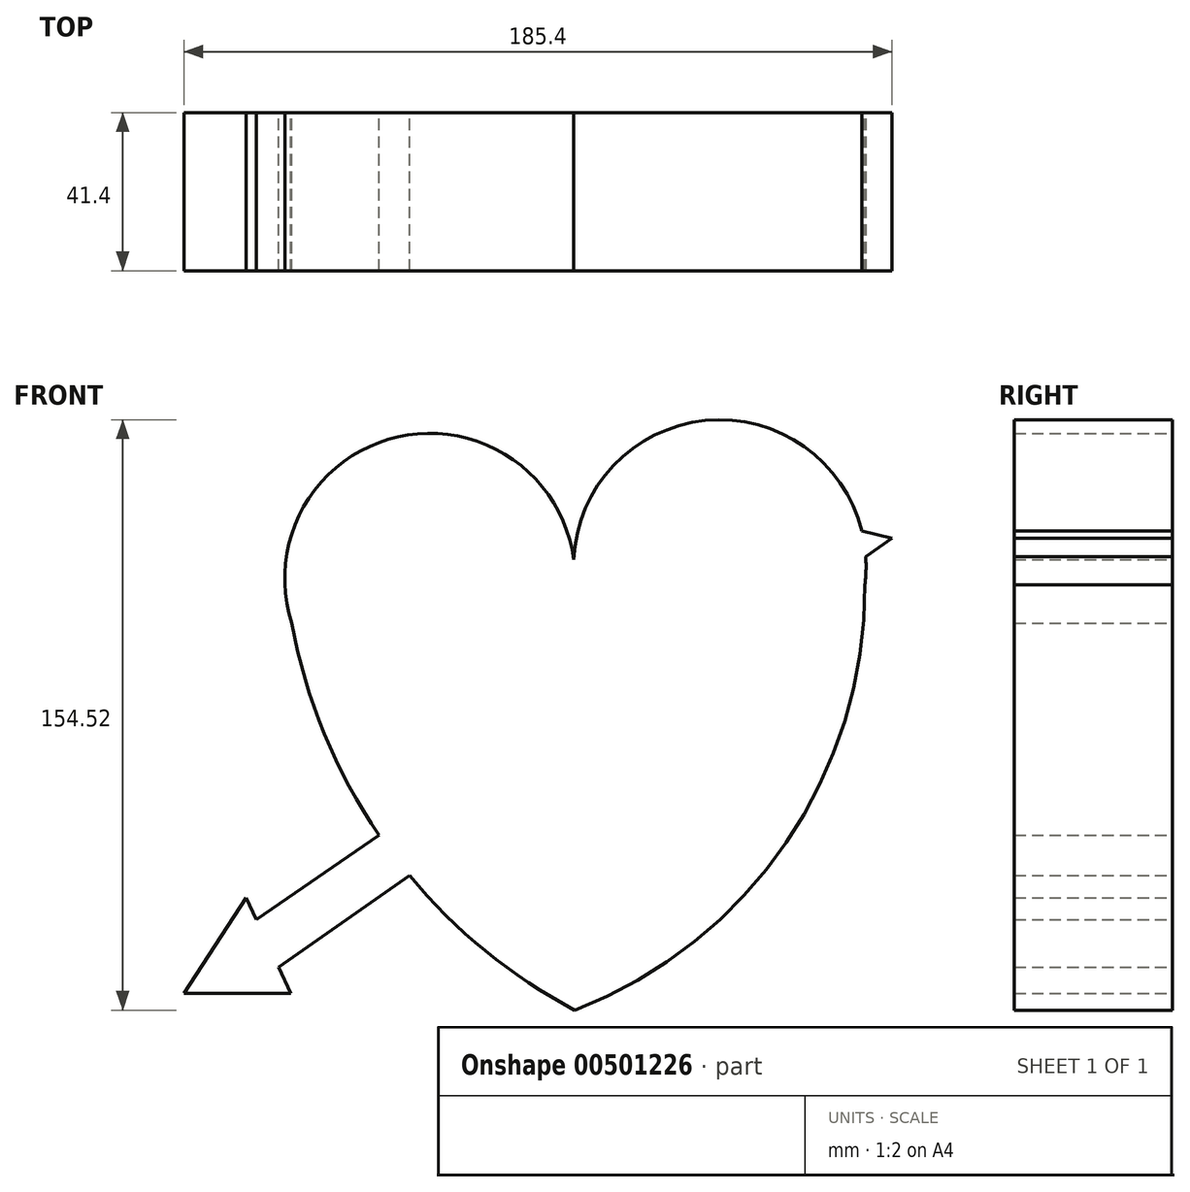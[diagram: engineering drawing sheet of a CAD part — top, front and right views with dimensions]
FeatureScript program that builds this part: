
annotation { "Feature Type Name" : "Feature", "Feature Type Description" : "" }
export const myFeature = defineFeature(function(context is Context, id is Id, definition is map)
    precondition{}
    {
        {
            var Q0;
            Q0=qCreatedBy(makeId("Front.planeOp"),FACE);
            var sketch = newSketch(context, id + "F0", { "sketchPlane" : qUnion([Q0])});
            skArc(sketch, "E0", {"start": v(0, 34.82) * mm, "mid": v(-43.02, 74.15) * mm, "end": v(-74.08, 24.83) * mm});
            skArc(sketch, "E1", {"start": v(75.92, 34.82) * mm, "mid": v(37.96, 78.02) * mm, "end": v(0, 34.82) * mm});
            skArc(sketch, "E2", {"start": v(-74.08, 24.83) * mm, "mid": v(-48.66, -34.34) * mm, "end": v(0, -76.5) * mm});
            skArc(sketch, "E3", {"start": v(0, -76.5) * mm, "mid": v(55.3, -32.67) * mm, "end": v(75.92, 34.82) * mm});
            skLineSegment(sketch, "E4", {"start": v(75.12, 48.9) * mm, "end": v(101.11, 42.78) * mm});
            skLineSegment(sketch, "E5", {"start": v(75.12, 48.9) * mm, "end": v(80.76, 72.86) * mm});
            skLineSegment(sketch, "E6", {"start": v(101.72, 50.63) * mm, "end": v(111.6, 48.9) * mm});
            skLineSegment(sketch, "E7", {"start": v(101.72, 50.63) * mm, "end": v(106.06, 75.42) * mm});
            skLineSegment(sketch, "E8", {"start": v(91.57, 60.13) * mm, "end": v(94.25, 75.42) * mm});
            skLineSegment(sketch, "E9", {"start": v(91.57, 60.13) * mm, "end": v(109.23, 57.04) * mm});
            skLineSegment(sketch, "E10", {"start": v(-86.07, -47.1) * mm, "end": v(-102.33, -72.12) * mm});
            skLineSegment(sketch, "E11", {"start": v(-102.33, -72.12) * mm, "end": v(-74.3, -72.12) * mm});
            skLineSegment(sketch, "E12", {"start": v(-74.3, -72.12) * mm, "end": v(-86.07, -47.1) * mm});
            skLineSegment(sketch, "E13", {"start": v(-83.38, -52.8) * mm, "end": v(67.56, 50.63) * mm});
            skLineSegment(sketch, "E14", {"start": v(-77.55, -65.2) * mm, "end": v(83.07, 47.03) * mm});
            skLineSegment(sketch, "E15", {"start": v(83.07, 47.03) * mm, "end": v(67.56, 50.63) * mm});
            skSolve(sketch);
        }
        {
            var Q0;
            Q0 = qSketchRegion(id + "F0", true);
            extrude(context, id + "F1", {"entities" : qUnion([Q0]), "depth" : 41.4 * mm, "offsetDistance" : 25.4 * mm});
        }
    });
